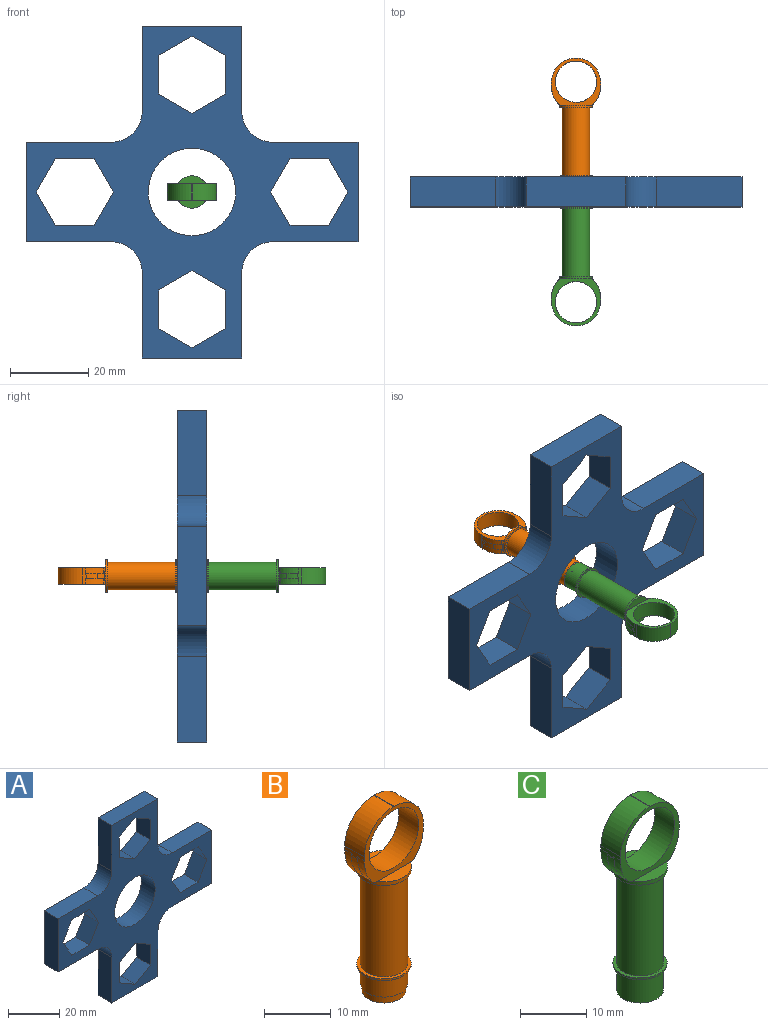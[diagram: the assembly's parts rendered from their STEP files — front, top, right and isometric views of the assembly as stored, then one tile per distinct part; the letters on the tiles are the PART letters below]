
ASSEMBLY  parts=3 mates=2
PART A: 43 faces, bbox 84.6x7.6x84.6 mm
  f0: plane 8.5x7.62mm, normal (-0.5,0,-0.87), area 74.8mm2, adj f1,f36,f37,f38
  f1: plane 9.81x7.62mm, normal (-1,0,0), area 74.8mm2, adj f0,f2,f37,f38
  f2: plane 8.5x7.62mm, normal (-0.5,0,0.87), area 74.8mm2, adj f1,f3,f37,f38
  f3: plane 8.5x7.62mm, normal (0.5,0,0.87), area 74.8mm2, adj f2,f4,f37,f38
  f4: plane 9.81x7.62mm, normal (1,0,0), area 74.8mm2, adj f3,f36,f37,f38
  f5: plane 8.5x7.62mm, normal (0.87,0,-0.5), area 74.8mm2, adj f6,f31,f37,f38
  f6: plane 9.81x7.62mm, normal (0,0,-1), area 74.8mm2, adj f5,f7,f37,f38
  f7: plane 8.5x7.62mm, normal (-0.87,0,-0.5), area 74.8mm2, adj f6,f8,f37,f38
  f8: plane 8.5x7.62mm, normal (-0.87,0,0.5), area 74.8mm2, adj f7,f9,f37,f38
  f9: plane 9.81x7.62mm, normal (0,0,1), area 74.8mm2, adj f8,f31,f37,f38
  f10: plane 8.5x7.62mm, normal (0.5,0,0.87), area 74.8mm2, adj f11,f32,f37,f38
  f11: plane 9.81x7.62mm, normal (1,0,0), area 74.8mm2, adj f10,f12,f37,f38
  f12: plane 8.5x7.62mm, normal (0.5,0,-0.87), area 74.8mm2, adj f11,f13,f37,f38
  f13: plane 8.5x7.62mm, normal (-0.5,0,-0.87), area 74.8mm2, adj f12,f14,f37,f38
  f14: plane 9.81x7.62mm, normal (-1,0,0), area 74.8mm2, adj f13,f32,f37,f38
  f15: plane 8.5x7.62mm, normal (-0.87,0,0.5), area 74.8mm2, adj f16,f34,f37,f38
  f16: plane 9.81x7.62mm, normal (0,0,1), area 74.8mm2, adj f15,f17,f37,f38
  f17: plane 8.5x7.62mm, normal (0.87,0,0.5), area 74.8mm2, adj f16,f18,f37,f38
  f18: plane 8.5x7.62mm, normal (0.87,0,-0.5), area 74.8mm2, adj f17,f19,f37,f38
  f19: plane 9.81x7.62mm, normal (0,0,-1), area 74.8mm2, adj f18,f34,f37,f38
  f20: plane 21.76x7.62mm, normal (0,0,1), area 165.8mm2, adj f35,f37,f38,f40
  f21: plane 21.76x7.62mm, normal (1,0,0), area 165.8mm2, adj f22,f37,f38,f40
  f22: plane 25.4x7.62mm, normal (0,0,1), area 193.5mm2, adj f21,f23,f37,f38
  f23: plane 21.76x7.62mm, normal (-1,0,0), area 165.8mm2, adj f22,f37,f38,f41
  f24: plane 21.76x7.62mm, normal (0,0,1), area 165.8mm2, adj f25,f37,f38,f41
  f25: plane 25.4x7.62mm, normal (-1,0,0), area 193.5mm2, adj f24,f26,f37,f38
  f26: plane 21.76x7.62mm, normal (0,0,-1), area 165.8mm2, adj f25,f37,f38,f39
  f27: plane 21.76x7.62mm, normal (-1,0,0), area 165.8mm2, adj f28,f37,f38,f39
  f28: plane 25.4x7.62mm, normal (0,0,-1), area 193.5mm2, adj f27,f29,f37,f38
  f29: plane 21.76x7.62mm, normal (1,0,0), area 165.8mm2, adj f28,f37,f38,f42
  f30: plane 21.76x7.62mm, normal (0,0,-1), area 165.8mm2, adj f35,f37,f38,f42
  f31: plane 8.5x7.62mm, normal (0.87,0,0.5), area 74.8mm2, adj f5,f9,f37,f38
  f32: plane 8.5x7.62mm, normal (-0.5,0,0.87), area 74.8mm2, adj f10,f14,f37,f38
  f33: cylinder r=11.14mm len=22.27mm, axis (0,1,0), area 533.1mm2, adj f37,f38
  f34: plane 8.5x7.62mm, normal (-0.87,0,-0.5), area 74.8mm2, adj f15,f19,f37,f38
  f35: plane 25.4x7.62mm, normal (1,0,0), area 193.5mm2, adj f20,f30,f37,f38
  f36: plane 8.5x7.62mm, normal (0.5,0,-0.87), area 74.8mm2, adj f0,f4,f37,f38
  f37: plane 84.62x84.62mm, normal (0,-1,0), area 2316.4mm2, adj f0,f1,f2,f3,f4,f5,f6,f7
  f38: plane 84.62x84.62mm, normal (0,1,0), area 2316.4mm2, adj f0,f1,f2,f3,f4,f5,f6,f7
  f39: cylinder r=7.85mm len=7.85mm, axis (0,1,0), area 93.9mm2, adj f26,f27,f37,f38
  f40: cylinder r=7.85mm len=7.85mm, axis (0,-1,0), area 93.9mm2, adj f20,f21,f37,f38
  f41: cylinder r=7.85mm len=7.85mm, axis (0,1,0), area 93.9mm2, adj f23,f24,f37,f38
  f42: cylinder r=7.85mm len=7.85mm, axis (0,1,0), area 93.9mm2, adj f29,f30,f37,f38
PART B: 35 faces, bbox 12.6x8.3x35 mm
  f0: plane 7.14x2.05mm, normal (0,0,1), area 10.2mm2, adj f4,f12
  f1: plane 7.09x2.03mm, normal (0,0,1), area 10.2mm2, adj f4,f22
  f2: bspline ~8.2x5.97mm, area 8.3mm2, adj f4,f7,f17,f21,f24,f26
  f3: cylinder r=3.54mm len=17.2mm, axis (0,0,-1), area 383.1mm2, adj f5,f29
  f4: cylinder r=4.11mm len=8.22mm, axis (0,0,1), area 17.1mm2, adj f0,f1,f2,f5,f11,f15,f16,f19
  f5: plane 8.22x8.22mm, normal (0,0,-1), area 13.6mm2, adj f3,f4
  f6: plane 4.17x0.13mm, normal (0,0,1), area 0.6mm2, adj f9,f10,f12,f22
  f7: plane 4.25x1.21mm, normal (1,0,0), area 3.1mm2, adj f2,f9,f12,f14,f21,f22
  f8: plane 4.24x1.2mm, normal (-1,0,0), area 3.1mm2, adj f10,f11,f12,f13,f18,f22
  f9: cylinder r=6.19mm len=6.19mm, axis (0,-1,0), area 40.6mm2, adj f6,f7,f12,f22
  f10: cylinder r=6.19mm len=6.19mm, axis (0,1,0), area 40.6mm2, adj f6,f8,f12,f22
  f11: bspline ~8.18x5.87mm, area 8.5mm2, adj f4,f8,f13,f18,f25,f27
  f12: plane 12.55x12.04mm, normal (0,1,0), area 40.1mm2, adj f0,f6,f7,f8,f9,f10,f13,f14
  f13: extruded ~4.82x1.84mm, area 7.4mm2, adj f8,f11,f12,f25
  f14: extruded ~4.82x1.84mm, area 7.3mm2, adj f7,f12,f17,f24
  f15: plane 0.1x0.06mm, normal (0,0,-1), area 0mm2, adj f4,f12,f25
  f16: plane 0.1x0.06mm, normal (0,0,-1), area 0mm2, adj f4,f12,f24
  f17: extruded ~4.82x1.84mm, area 0mm2, adj f2,f14
  f18: extruded ~4.82x1.84mm, area 7.4mm2, adj f8,f11,f22,f27
  f19: plane 0.1x0.06mm, normal (0,0,-1), area 0mm2, adj f4,f22,f27
  f20: plane 0.1x0.06mm, normal (0,0,-1), area 0mm2, adj f4,f22,f26
  f21: extruded ~4.82x1.84mm, area 7.4mm2, adj f2,f7,f22,f26
  f22: plane 12.55x12.04mm, normal (0,-1,0), area 40.1mm2, adj f1,f6,f7,f8,f9,f10,f18,f19
  f23: cylinder r=5.27mm len=10.54mm, axis (0,-1,0), area 138.1mm2, adj f12,f22
  f24: cylinder r=1.17mm len=1.38mm, axis (0,1,0), area 0.8mm2, adj f2,f12,f14,f16
  f25: cylinder r=1.17mm len=1.4mm, axis (0,1,0), area 0.8mm2, adj f11,f12,f13,f15
  f26: cylinder r=1.17mm len=1.4mm, axis (0,1,0), area 0.8mm2, adj f2,f20,f21,f22
  f27: cylinder r=1.17mm len=1.4mm, axis (0,1,0), area 0.8mm2, adj f11,f18,f19,f22
  f28: cylinder r=4.08mm len=8.16mm, axis (0,0,-1), area 7.9mm2, adj f29,f31
  f29: plane 8.16x8.16mm, normal (0,0,1), area 12.8mm2, adj f3,f28
  f30: cylinder r=3.54mm len=7.09mm, axis (0,0,-1), area 76.2mm2, adj f31,f34
  f31: plane 8.16x8.16mm, normal (0,0,-1), area 12.8mm2, adj f28,f30
  f32: plane 6.58x6.58mm, normal (0,0,-1), area 34mm2, adj f33
  f33: cylinder r=3.29mm len=6.58mm, axis (0,0,-1), area 26.3mm2, adj f32,f34
  f34: plane 7.09x7.09mm, normal (0,0,-1), area 5.5mm2, adj f30,f33
PART C: 35 faces, bbox 12.6x8.3x35 mm
  f0: plane 7.14x2.05mm, normal (0,0,1), area 10.2mm2, adj f4,f12
  f1: plane 7.09x2.03mm, normal (0,0,1), area 10.2mm2, adj f4,f22
  f2: bspline ~8.2x5.97mm, area 8.3mm2, adj f4,f7,f17,f21,f24,f26
  f3: cylinder r=3.54mm len=17.2mm, axis (0,0,-1), area 383.1mm2, adj f5,f29
  f4: cylinder r=4.11mm len=8.22mm, axis (0,0,1), area 17.1mm2, adj f0,f1,f2,f5,f11,f15,f16,f19
  f5: plane 8.22x8.22mm, normal (0,0,-1), area 13.6mm2, adj f3,f4
  f6: plane 4.17x0.13mm, normal (0,0,1), area 0.6mm2, adj f9,f10,f12,f22
  f7: plane 4.25x1.21mm, normal (1,0,0), area 3.1mm2, adj f2,f9,f12,f14,f21,f22
  f8: plane 4.24x1.2mm, normal (-1,0,0), area 3.1mm2, adj f10,f11,f12,f13,f18,f22
  f9: cylinder r=6.19mm len=6.19mm, axis (0,-1,0), area 40.6mm2, adj f6,f7,f12,f22
  f10: cylinder r=6.19mm len=6.19mm, axis (0,1,0), area 40.6mm2, adj f6,f8,f12,f22
  f11: bspline ~8.18x5.87mm, area 8.5mm2, adj f4,f8,f13,f18,f25,f27
  f12: plane 12.55x12.04mm, normal (0,1,0), area 40.1mm2, adj f0,f6,f7,f8,f9,f10,f13,f14
  f13: extruded ~4.82x1.84mm, area 7.4mm2, adj f8,f11,f12,f25
  f14: extruded ~4.82x1.84mm, area 7.3mm2, adj f7,f12,f17,f24
  f15: plane 0.1x0.06mm, normal (0,0,-1), area 0mm2, adj f4,f12,f25
  f16: plane 0.1x0.06mm, normal (0,0,-1), area 0mm2, adj f4,f12,f24
  f17: extruded ~4.82x1.84mm, area 0mm2, adj f2,f14
  f18: extruded ~4.82x1.84mm, area 7.4mm2, adj f8,f11,f22,f27
  f19: plane 0.1x0.05mm, normal (0,0,-1), area 0mm2, adj f4,f22,f27
  f20: plane 0.1x0.06mm, normal (0,0,-1), area 0mm2, adj f4,f22,f26
  f21: extruded ~4.82x1.84mm, area 7.4mm2, adj f2,f7,f22,f26
  f22: plane 12.55x12.04mm, normal (0,-1,0), area 40.1mm2, adj f1,f6,f7,f8,f9,f10,f18,f19
  f23: cylinder r=5.27mm len=10.54mm, axis (0,-1,0), area 138.1mm2, adj f12,f22
  f24: cylinder r=1.17mm len=1.38mm, axis (0,1,0), area 0.8mm2, adj f2,f12,f14,f16
  f25: cylinder r=1.17mm len=1.4mm, axis (0,1,0), area 0.8mm2, adj f11,f12,f13,f15
  f26: cylinder r=1.17mm len=1.4mm, axis (0,1,0), area 0.8mm2, adj f2,f20,f21,f22
  f27: cylinder r=1.17mm len=1.4mm, axis (0,1,0), area 0.8mm2, adj f11,f18,f19,f22
  f28: cylinder r=4.08mm len=8.16mm, axis (0,0,-1), area 7.9mm2, adj f29,f31
  f29: plane 8.16x8.16mm, normal (0,0,1), area 12.8mm2, adj f3,f28
  f30: cylinder r=3.54mm len=7.09mm, axis (0,0,-1), area 104.5mm2, adj f31,f34
  f31: plane 8.16x8.16mm, normal (0,0,-1), area 12.8mm2, adj f28,f30
  f32: plane 6.58x6.58mm, normal (0,0,-1), area 34mm2, adj f33
  f33: cylinder r=3.29mm len=6.58mm, axis (0,0,-1), area 26.3mm2, adj f32,f34
  f34: plane 7.09x7.09mm, normal (0,0,-1), area 5.5mm2, adj f30,f33
PLACE A t=(-10.09,-7.84,-1.45)mm
PLACE B rot(axis=(-1,0,0),90deg) t=(94.71,-3.52,68.41)mm
PLACE C rot(axis=(1,0,0),90deg) t=(94.71,-12.15,-20.66)mm
MATE fastened C.f3 <-> A.f33  axis (0,1,0) through (28.7,-7.07,23.88)mm
MATE fastened B.f3 <-> A.f33  axis (0,-1,0) through (28.7,-8.6,23.88)mm
